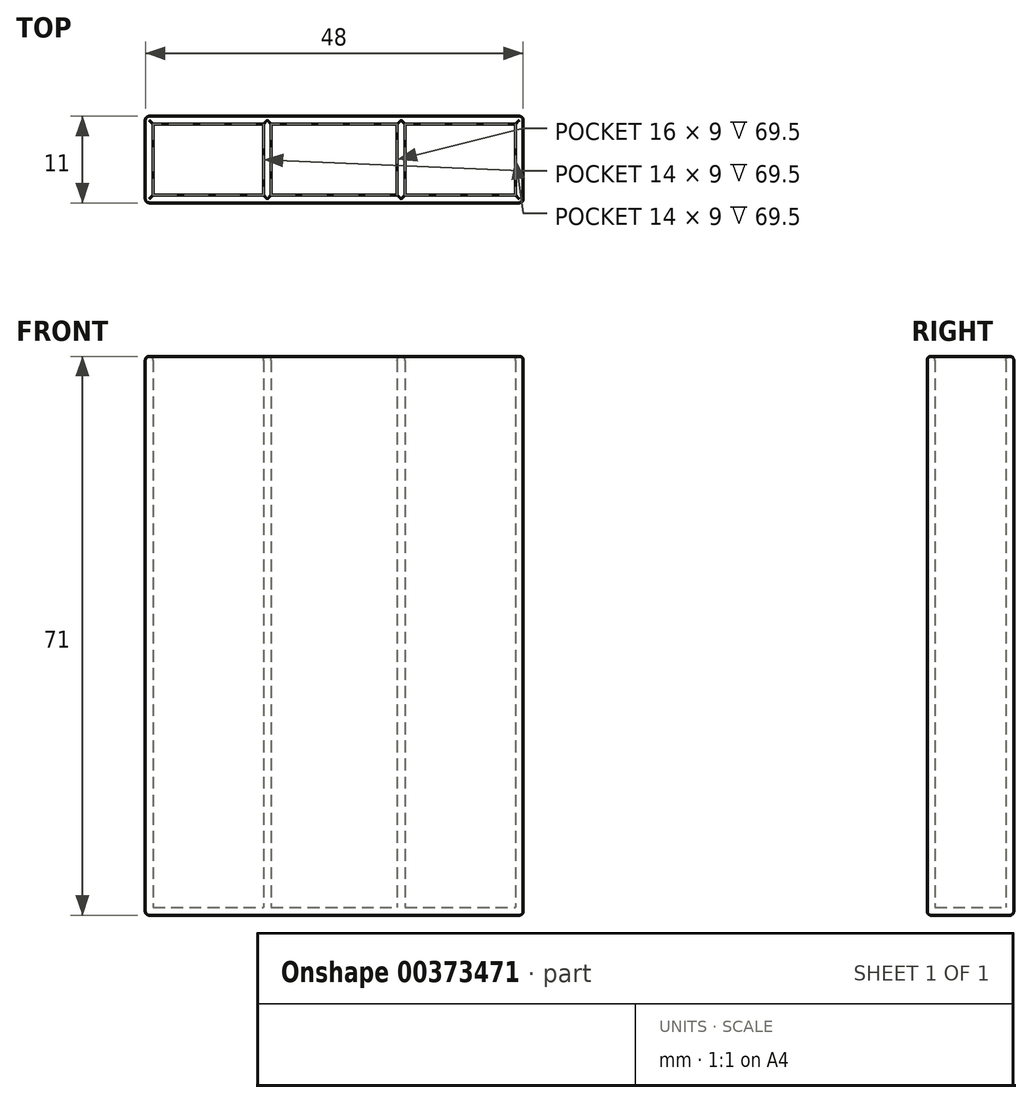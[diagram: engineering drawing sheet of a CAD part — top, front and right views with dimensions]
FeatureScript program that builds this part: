
annotation { "Feature Type Name" : "Feature", "Feature Type Description" : "" }
export const myFeature = defineFeature(function(context is Context, id is Id, definition is map)
    precondition{}
    {
        {
            var Q0;
            Q0=qCreatedBy(makeId("Top.planeOp"),FACE);
            var sketch = newSketch(context, id + "F0", { "sketchPlane" : qUnion([Q0])});
            skLineSegment(sketch, "E0.bottom", {"start": v(-19.07, 0) * mm, "end": v(28.93, 0) * mm});
            skLineSegment(sketch, "E0.top", {"start": v(-19.07, 11) * mm, "end": v(28.93, 11) * mm});
            skLineSegment(sketch, "E0.left", {"start": v(-19.07, 0) * mm, "end": v(-19.07, 11) * mm});
            skLineSegment(sketch, "E0.right", {"start": v(28.93, 0) * mm, "end": v(28.93, 11) * mm});
            skLineSegment(sketch, "E1.0", {"start": v(-18.07, 10) * mm, "end": v(27.93, 10) * mm});
            skLineSegment(sketch, "E1.1", {"start": v(-18.07, 1) * mm, "end": v(-18.07, 10) * mm});
            skLineSegment(sketch, "E1.2", {"start": v(-18.07, 1) * mm, "end": v(27.93, 1) * mm});
            skLineSegment(sketch, "E1.3", {"start": v(27.93, 1) * mm, "end": v(27.93, 10) * mm});
            skLineSegment(sketch, "E2", {"start": v(-4.07, 10) * mm, "end": v(-4.07, 1) * mm});
            skLineSegment(sketch, "E3", {"start": v(13.93, 10) * mm, "end": v(13.93, 1) * mm});
            skLineSegment(sketch, "E4.0", {"start": v(-3.07, 10) * mm, "end": v(-3.07, 1) * mm});
            skLineSegment(sketch, "E5.0", {"start": v(12.93, 10) * mm, "end": v(12.93, 1) * mm});
            skSolve(sketch);
        }
        {
            var Q0;
            Q0=makeQuery(id+"F0.imprint","IMPRINT",FACE,{"disambiguationData":[TD([[makeQuery(id+"F0.imprint","IMPRINT",EDGE,{"derivedFrom":sQuery(id+"F0.wireOp",EDGE,"E1.0")}),-1.0]])]});
            extrude(context, id + "F1", {"entities" : qUnion([Q0]), "depth" : 1 * mm});
        }
        {
            var Q0;
            Q0=makeQuery(id+"F0.imprint","IMPRINT",FACE,{"disambiguationData":[TD([[makeQuery(id+"F0.imprint","IMPRINT",EDGE,{"derivedFrom":sQuery(id+"F0.wireOp",EDGE,"E0.bottom")}),1.0]])]});
            extrude(context, id + "F2", {"entities" : qUnion([Q0]), "operationType" : NewBodyOperationType.ADD, "depth" : 71 * mm});
        }
        {
            var Q0;
            {var subQ0=sQuery(id+"F0.wireOp",EDGE,"E2");Q0=makeQuery(id+"F0.imprint","IMPRINT",FACE,{"disambiguationData":[TD([[makeQuery(id+"F0.imprint","IMPRINT",EDGE,{"derivedFrom":subQ0}),1.0]])]});}
            var Q1;
            {var subQ0=sQuery(id+"F0.wireOp",EDGE,"E3");Q1=makeQuery(id+"F0.imprint","IMPRINT",FACE,{"disambiguationData":[TD([[makeQuery(id+"F0.imprint","IMPRINT",EDGE,{"derivedFrom":subQ0}),-1.0]])]});}
            extrude(context, id + "F3", {"entities" : qUnion([Q0, Q1]), "operationType" : NewBodyOperationType.ADD, "depth" : 71 * mm});
        }
        {
            var Q0;
            {var subQ0=sQuery(id+"F0.wireOp",EDGE,"E1.2");var subQ1=sQuery(id+"F0.wireOp",EDGE,"E1.0");Q0=makeQuery(id+"F3.boolean.opBoolean","MERGE",FACE,{"derivedFrom":[makeQuery(id+"F2.opExtrude","CAP_FACE",FACE,{"disambiguationData":[OSD([sQuery(id+"F0.wireOp",EDGE,"E0.bottom"),sQuery(id+"F0.wireOp",EDGE,"E0.top"),sQuery(id+"F0.wireOp",EDGE,"E0.left"),sQuery(id+"F0.wireOp",EDGE,"E0.right"),subQ1,sQuery(id+"F0.wireOp",EDGE,"E1.1"),subQ0,sQuery(id+"F0.wireOp",EDGE,"E1.3")])],"isStart":false}),makeQuery(id+"F3.opExtrude","CAP_FACE",FACE,{"disambiguationData":[OSD([subQ1,subQ0,sQuery(id+"F0.wireOp",EDGE,"E2"),sQuery(id+"F0.wireOp",EDGE,"E4.0")])],"isStart":false}),makeQuery(id+"F3.opExtrude","CAP_FACE",FACE,{"disambiguationData":[OSD([subQ1,subQ0,sQuery(id+"F0.wireOp",EDGE,"E3"),sQuery(id+"F0.wireOp",EDGE,"E5.0")])],"isStart":false})]});}
            var Q1;
            Q1=makeQuery(id+"F2.opExtrude","SWEPT_FACE",FACE,{"disambiguationData":[OSD([sQuery(id+"F0.wireOp",EDGE,"E0.top")])]});
            var Q2;
            Q2=makeQuery(id+"F2.opExtrude","SWEPT_FACE",FACE,{"disambiguationData":[OSD([sQuery(id+"F0.wireOp",EDGE,"E0.left")])]});
            var Q3;
            Q3=makeQuery(id+"F2.opExtrude","SWEPT_FACE",FACE,{"disambiguationData":[OSD([sQuery(id+"F0.wireOp",EDGE,"E0.bottom")])]});
            var Q4;
            Q4=makeQuery(id+"F2.opExtrude","SWEPT_FACE",FACE,{"disambiguationData":[OSD([sQuery(id+"F0.wireOp",EDGE,"E0.right")])]});
            fillet(context, id + "F4", {"entities" : qUnion([Q0, Q1, Q2, Q3, Q4]), "radius" : 0.5 * mm, "tangentPropagation" : true, "allowEdgeOverflow" : false});
        }
    });
